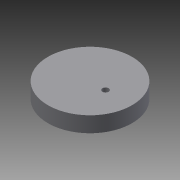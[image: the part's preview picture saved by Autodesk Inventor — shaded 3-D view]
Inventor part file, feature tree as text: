
AUTODESK INVENTOR PART (.ipt)
format: ipt  version: 2014 (Build 180170000, 170)  size: 75,776 bytes
history: native  units: in
note: dims shown in document units (in); Inventor stores cm internally (conversion verified against a paired STEP export)
features: extrude x2, sketch x2, other x1
ambient origin geometry x8: Origin, YZ Plane, XZ Plane, XY Plane, X Axis, Y Axis, Z Axis, Center Point
bodies: Body1 (feature_tree)
feature tree (5):
  other  "Sólido1"
  extrude  "Extrusión1"  Depth=0.1969in TaperAngle=0.0deg
  extrude  "Extrusión2"  Depth=0.1969in TaperAngle=0.0deg
  sketch  "Boceto1"  dims[d0=1.063in d1=0.1969in d2=0.0in]
  sketch  "Boceto3"  dims[d4=0.0787in d5=0.1969in d6=0.0in d7=0.1969in]
